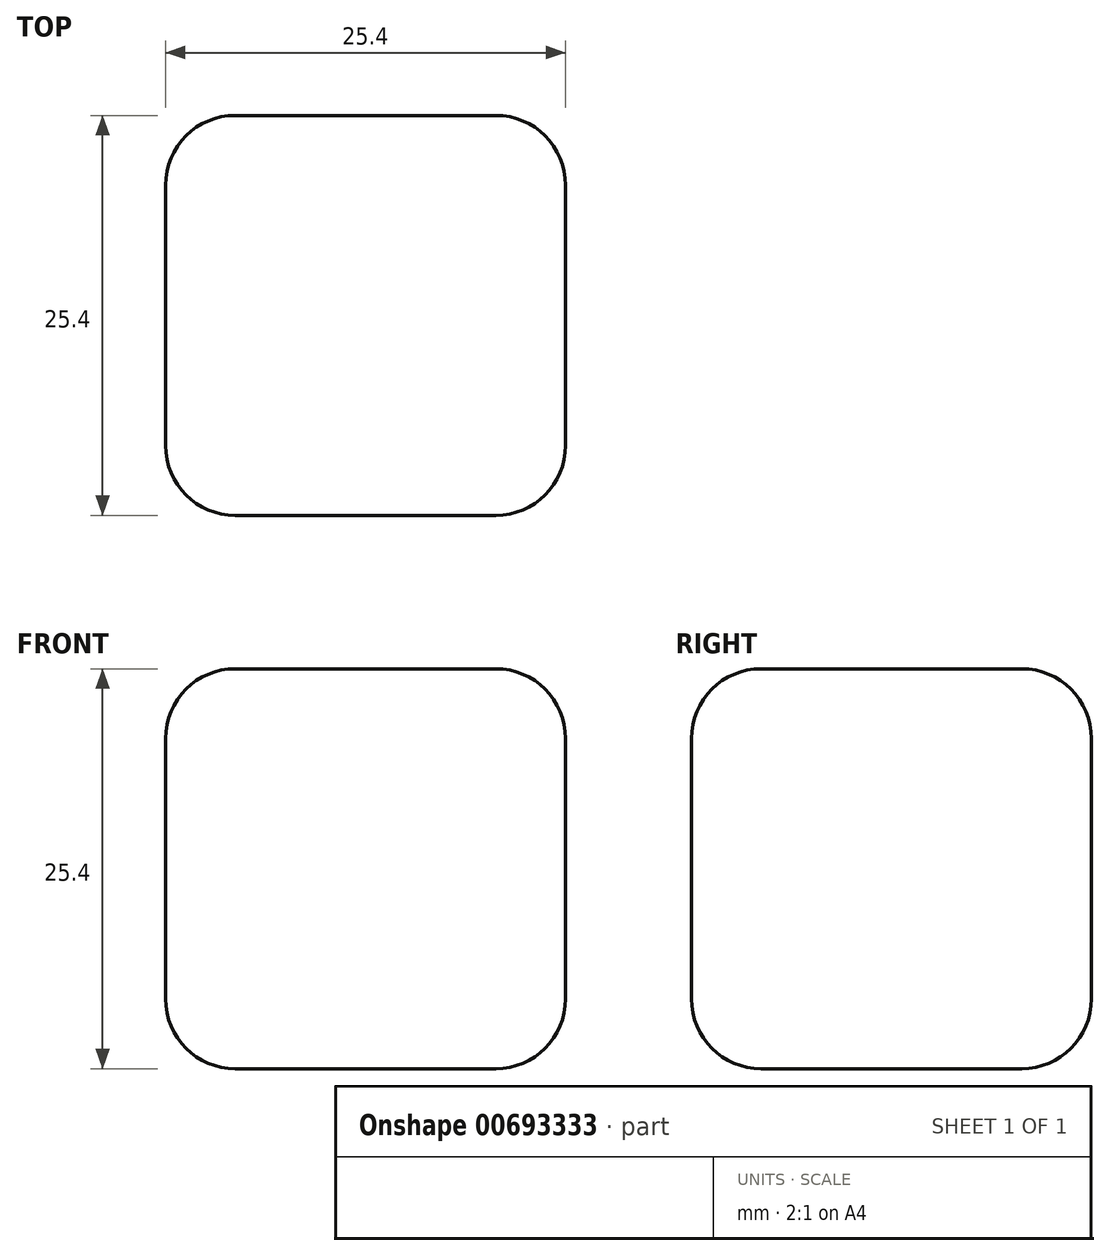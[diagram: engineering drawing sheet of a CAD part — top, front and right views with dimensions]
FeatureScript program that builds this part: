
annotation { "Feature Type Name" : "Feature", "Feature Type Description" : "" }
export const myFeature = defineFeature(function(context is Context, id is Id, definition is map)
    precondition{}
    {
        {
            var Q0;
            Q0=qCreatedBy(makeId("Right.planeOp"),FACE);
            var sketch = newSketch(context, id + "F0", { "sketchPlane" : qUnion([Q0])});
            skLineSegment(sketch, "E0.bottom", {"start": v(-10.98, 20.5) * mm, "end": v(14.42, 20.5) * mm});
            skLineSegment(sketch, "E0.top", {"start": v(-10.98, -4.9) * mm, "end": v(14.42, -4.9) * mm});
            skLineSegment(sketch, "E0.left", {"start": v(-10.98, 20.5) * mm, "end": v(-10.98, -4.9) * mm});
            skLineSegment(sketch, "E0.right", {"start": v(14.42, 20.5) * mm, "end": v(14.42, -4.9) * mm});
            skSolve(sketch);
        }
        {
            var Q0;
            Q0=makeQuery(id+"F0.imprint","IMPRINT",FACE,{"disambiguationData":[TD([[makeQuery(id+"F0.imprint","IMPRINT",EDGE,{"derivedFrom":sQuery(id+"F0.wireOp",EDGE,"E0.bottom")}),-1.0]])]});
            extrude(context, id + "F1", {"entities" : qUnion([Q0]), "depth" : 25.4 * mm, "offsetDistance" : 25.4 * mm});
        }
        {
            var Q0;
            Q0=makeQuery(id+"F1.opExtrude","SWEPT_EDGE",EDGE,{"disambiguationData":[OSD([sQuery(id+"F0.wireOp",EDGE,"E0.bottom"),sQuery(id+"F0.wireOp",EDGE,"E0.left")])]});
            var Q1;
            Q1=makeQuery(id+"F1.opExtrude","SWEPT_FACE",FACE,{"disambiguationData":[OSD([sQuery(id+"F0.wireOp",EDGE,"E0.bottom")])]});
            var Q2;
            Q2=makeQuery(id+"F1.opExtrude","CAP_FACE",FACE,{"disambiguationData":[OSD([sQuery(id+"F0.wireOp",EDGE,"E0.bottom"),sQuery(id+"F0.wireOp",EDGE,"E0.top"),sQuery(id+"F0.wireOp",EDGE,"E0.left"),sQuery(id+"F0.wireOp",EDGE,"E0.right")])],"isStart":false});
            var Q3;
            Q3=makeQuery(id+"F1.opExtrude","SWEPT_FACE",FACE,{"disambiguationData":[OSD([sQuery(id+"F0.wireOp",EDGE,"E0.left")])]});
            var Q4;
            Q4=makeQuery(id+"F1.opExtrude","SWEPT_FACE",FACE,{"disambiguationData":[OSD([sQuery(id+"F0.wireOp",EDGE,"E0.right")])]});
            var Q5;
            Q5=makeQuery(id+"F1.opExtrude","CAP_FACE",FACE,{"disambiguationData":[OSD([sQuery(id+"F0.wireOp",EDGE,"E0.bottom"),sQuery(id+"F0.wireOp",EDGE,"E0.top"),sQuery(id+"F0.wireOp",EDGE,"E0.left"),sQuery(id+"F0.wireOp",EDGE,"E0.right")])],"isStart":true});
            fillet(context, id + "F2", {"entities" : qUnion([Q0, Q1, Q2, Q3, Q4, Q5]), "radius" : 4.43 * mm, "allowEdgeOverflow" : false});
        }
    });
